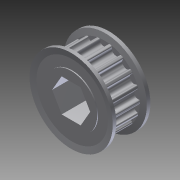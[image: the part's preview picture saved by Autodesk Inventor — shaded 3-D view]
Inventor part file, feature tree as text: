
AUTODESK INVENTOR PART (.ipt)
format: ipt  version: 2014 (Build 180170000, 170)  size: 652,800 bytes
history: native  units: in
note: dims shown in document units (in); Inventor stores cm internally (conversion verified against a paired STEP export)
features: mirror x1, other x1, imported_body x1
ambient origin geometry x8: Origin, YZ Plane, XZ Plane, XY Plane, X Axis, Y Axis, Z Axis, Center Point
bodies: Body1 (feature_tree)
feature tree (3):
  mirror  "Mirror1"
  other  "217-3225-STEP1"
  imported_body  "Base1"
